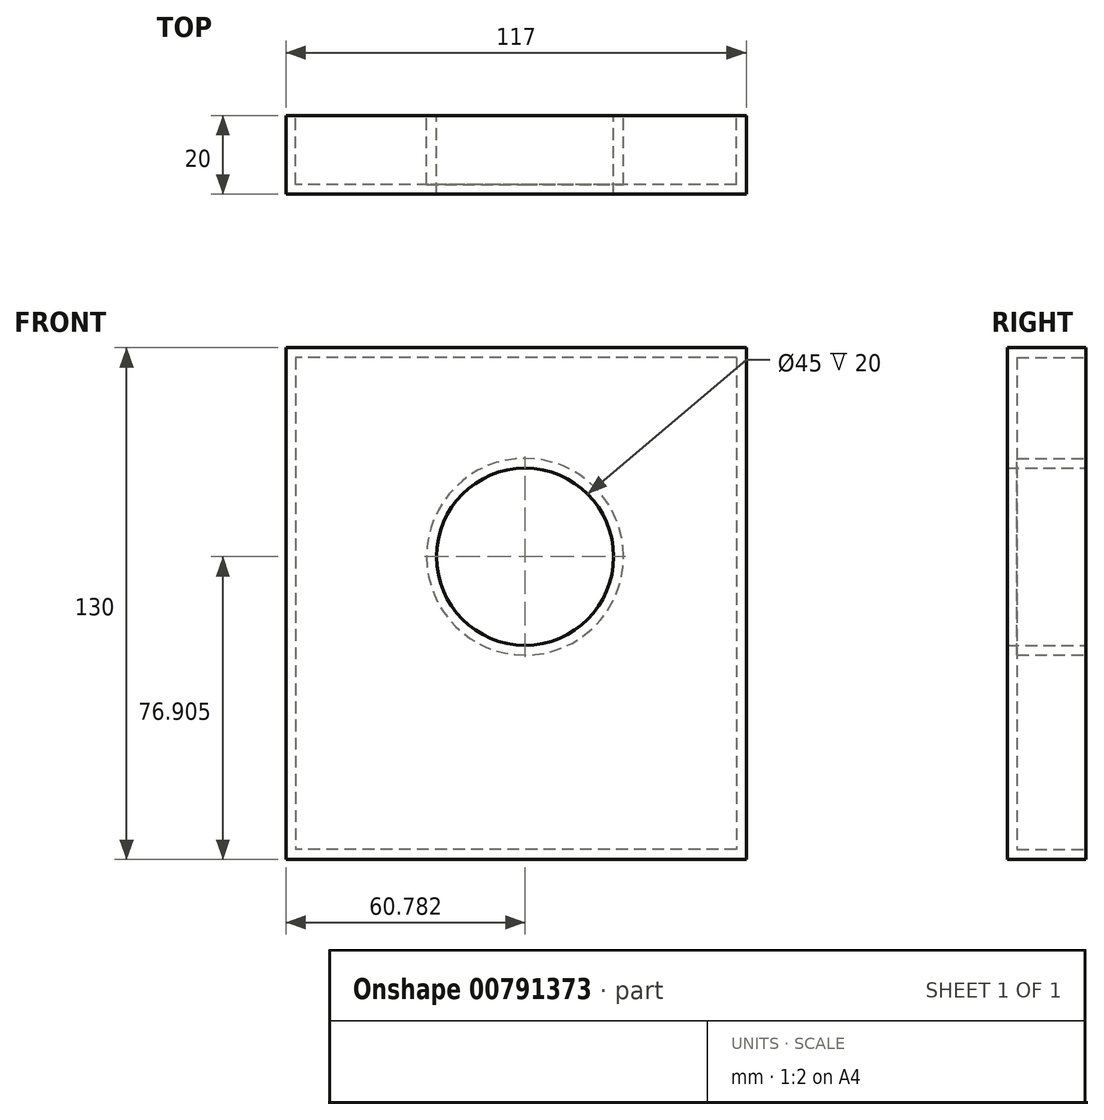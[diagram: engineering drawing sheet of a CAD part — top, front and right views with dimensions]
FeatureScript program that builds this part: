
annotation { "Feature Type Name" : "Feature", "Feature Type Description" : "" }
export const myFeature = defineFeature(function(context is Context, id is Id, definition is map)
    precondition{}
    {
        {
            var Q0;
            Q0=qCreatedBy(makeId("Front.planeOp"),FACE);
            var sketch = newSketch(context, id + "F0", { "sketchPlane" : qUnion([Q0])});
            skLineSegment(sketch, "E0.bottom", {"start": v(68.77, 68.3) * mm, "end": v(-48.23, 68.3) * mm});
            skLineSegment(sketch, "E0.top", {"start": v(68.77, -61.7) * mm, "end": v(-48.23, -61.7) * mm});
            skLineSegment(sketch, "E0.left", {"start": v(68.77, 68.3) * mm, "end": v(68.77, -61.7) * mm});
            skLineSegment(sketch, "E0.right", {"start": v(-48.23, 68.3) * mm, "end": v(-48.23, -61.7) * mm});
            skCircle(sketch, "E1", {"center": v(12.55, 15.2) * mm, "radius": 22.5 * mm});
            skSolve(sketch);
        }
        {
            var Q0;
            Q0 = qSketchRegion(id + "F0", true);
            extrude(context, id + "F1", {"entities" : qUnion([Q0]), "depth" : 20 * mm, "offsetDistance" : 25 * mm});
        }
        {
            var Q0;
            Q0=makeQuery(id+"F1.opExtrude","CAP_FACE",FACE,{"disambiguationData":[OSD([sQuery(id+"F0.wireOp",EDGE,"E0.bottom"),sQuery(id+"F0.wireOp",EDGE,"E0.top"),sQuery(id+"F0.wireOp",EDGE,"E0.left"),sQuery(id+"F0.wireOp",EDGE,"E0.right"),sQuery(id+"F0.wireOp",EDGE,"E1")])],"isStart":true});
            shell(context, id + "F2", {"entities" : qUnion([Q0]), "thickness" : 2.5 * mm});
        }
    });
